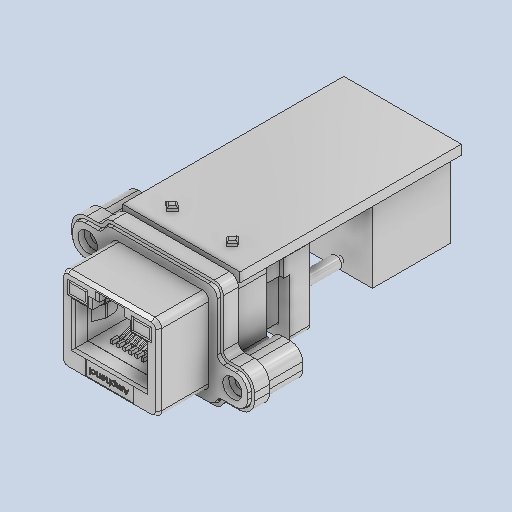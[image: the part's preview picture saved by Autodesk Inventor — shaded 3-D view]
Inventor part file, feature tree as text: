
AUTODESK INVENTOR PART (.ipt)
format: ipt  version: 2024.2 (Build 282272000, 272)  size: 974,336 bytes
history: native  units: mm
features: extrude x2, other x1
ambient origin geometry x8: Origin, YZ Plane, XZ Plane, XY Plane, X Axis, Y Axis, Z Axis, Center Point
bodies: Solid1 (feature_tree)
feature tree (3):
  extrude  "Extrusion1"  Depth=16.0mm
  extrude  "Extrusion2"  Depth=19.5mm
  other  "Boss-Extrude1"
